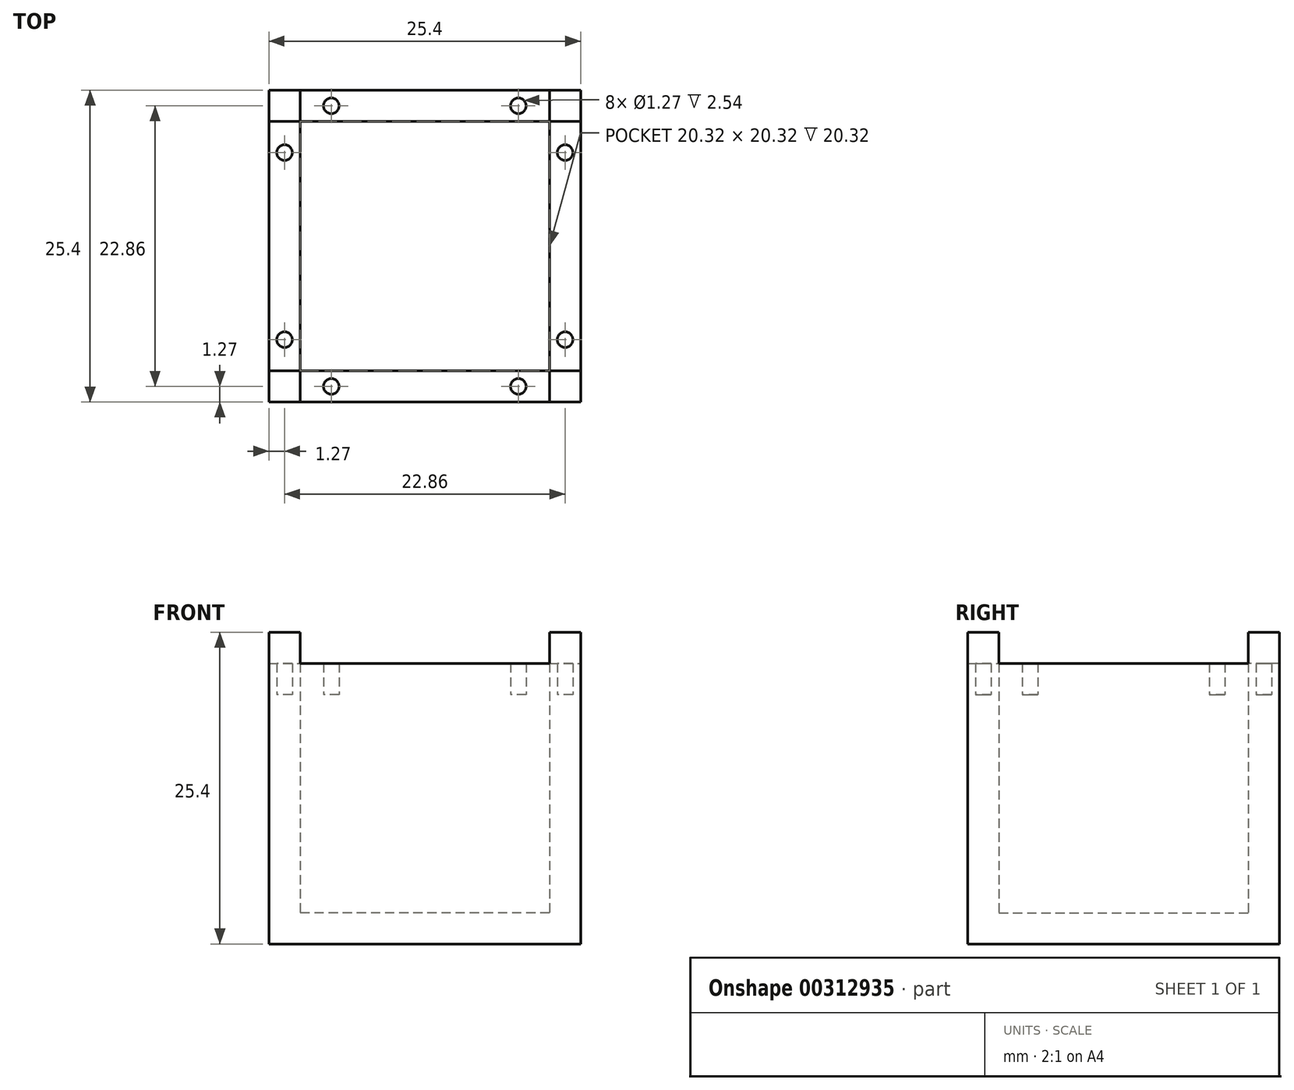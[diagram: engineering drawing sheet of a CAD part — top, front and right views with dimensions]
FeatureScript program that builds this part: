
annotation { "Feature Type Name" : "Feature", "Feature Type Description" : "" }
export const myFeature = defineFeature(function(context is Context, id is Id, definition is map)
    precondition{}
    {
        {
            var Q0;
            Q0=qCreatedBy(makeId("Top.planeOp"),FACE);
            var sketch = newSketch(context, id + "F0", { "sketchPlane" : qUnion([Q0])});
            skLineSegment(sketch, "E0.bottom", {"start": v(12.7, -12.7) * mm, "end": v(-12.7, -12.7) * mm});
            skLineSegment(sketch, "E0.top", {"start": v(12.7, 12.7) * mm, "end": v(-12.7, 12.7) * mm});
            skLineSegment(sketch, "E0.left", {"start": v(12.7, -12.7) * mm, "end": v(12.7, 12.7) * mm});
            skLineSegment(sketch, "E0.right", {"start": v(-12.7, -12.7) * mm, "end": v(-12.7, 12.7) * mm});
            skPoint(sketch, "E0.middle", {"position": v(0, 0) * mm});
            skLineSegment(sketch, "E1.bottom", {"start": v(10.16, -10.16) * mm, "end": v(-10.16, -10.16) * mm});
            skLineSegment(sketch, "E1.top", {"start": v(10.16, 10.16) * mm, "end": v(-10.16, 10.16) * mm});
            skLineSegment(sketch, "E1.left", {"start": v(10.16, -10.16) * mm, "end": v(10.16, 10.16) * mm});
            skLineSegment(sketch, "E1.right", {"start": v(-10.16, -10.16) * mm, "end": v(-10.16, 10.16) * mm});
            skLineSegment(sketch, "E2", {"start": v(-10.16, 10.16) * mm, "end": v(-10.16, 12.7) * mm});
            skLineSegment(sketch, "E3", {"start": v(-10.16, 10.16) * mm, "end": v(-12.7, 10.16) * mm});
            skLineSegment(sketch, "E4", {"start": v(-12.7, 10.16) * mm, "end": v(-12.7, 12.7) * mm});
            skLineSegment(sketch, "E5", {"start": v(10.16, 10.16) * mm, "end": v(10.16, 12.7) * mm});
            skLineSegment(sketch, "E6", {"start": v(10.16, 12.7) * mm, "end": v(12.7, 12.7) * mm});
            skLineSegment(sketch, "E7", {"start": v(12.7, 10.16) * mm, "end": v(10.16, 10.16) * mm});
            skLineSegment(sketch, "E8.bottom", {"start": v(-10.16, -10.16) * mm, "end": v(-12.7, -10.16) * mm});
            skLineSegment(sketch, "E8.top", {"start": v(-10.16, -12.7) * mm, "end": v(-12.7, -12.7) * mm});
            skLineSegment(sketch, "E8.left", {"start": v(-10.16, -10.16) * mm, "end": v(-10.16, -12.7) * mm});
            skLineSegment(sketch, "E8.right", {"start": v(-12.7, -10.16) * mm, "end": v(-12.7, -12.7) * mm});
            skLineSegment(sketch, "E9.bottom", {"start": v(10.16, -10.16) * mm, "end": v(12.7, -10.16) * mm});
            skLineSegment(sketch, "E9.top", {"start": v(10.16, -12.7) * mm, "end": v(12.7, -12.7) * mm});
            skLineSegment(sketch, "E9.left", {"start": v(10.16, -10.16) * mm, "end": v(10.16, -12.7) * mm});
            skLineSegment(sketch, "E9.right", {"start": v(12.7, -10.16) * mm, "end": v(12.7, -12.7) * mm});
            skSolve(sketch);
        }
        {
            var Q0;
            Q0=makeQuery(id+"F0.imprint","IMPRINT",FACE,{"disambiguationData":[TD([[makeQuery(id+"F0.imprint","IMPRINT",EDGE,{"derivedFrom":sQuery(id+"F0.wireOp",EDGE,"E1.bottom")}),-1.0]])]});
            extrude(context, id + "F1", {"entities" : qUnion([Q0]), "depth" : 2.54 * mm});
        }
        {
            var Q0;
            Q0=makeQuery(id+"F0.imprint","IMPRINT",FACE,{"disambiguationData":[TD([[makeQuery(id+"F0.imprint","IMPRINT",EDGE,{"derivedFrom":sQuery(id+"F0.wireOp",EDGE,"E0.right")}),-1.0]])]});
            var Q1;
            {var subQ2=sQuery(id+"F0.wireOp",EDGE,"E2");Q1=makeQuery(id+"F0.imprint","IMPRINT",FACE,{"disambiguationData":[TD([[makeQuery(id+"F0.imprint","IMPRINT",EDGE,{"derivedFrom":subQ2}),1.0]])]});}
            var Q2;
            Q2=makeQuery(id+"F0.imprint","IMPRINT",FACE,{"disambiguationData":[TD([[makeQuery(id+"F0.imprint","IMPRINT",EDGE,{"derivedFrom":sQuery(id+"F0.wireOp",EDGE,"E1.top")}),-1.0]])]});
            var Q3;
            Q3=makeQuery(id+"F0.imprint","IMPRINT",FACE,{"disambiguationData":[TD([[makeQuery(id+"F0.imprint","IMPRINT",EDGE,{"derivedFrom":sQuery(id+"F0.wireOp",EDGE,"E5")}),-1.0]])]});
            var Q4;
            Q4=makeQuery(id+"F0.imprint","IMPRINT",FACE,{"disambiguationData":[TD([[makeQuery(id+"F0.imprint","IMPRINT",EDGE,{"derivedFrom":sQuery(id+"F0.wireOp",EDGE,"E1.left")}),-1.0]])]});
            var Q5;
            Q5=makeQuery(id+"F0.imprint","IMPRINT",FACE,{"disambiguationData":[TD([[makeQuery(id+"F0.imprint","IMPRINT",EDGE,{"derivedFrom":sQuery(id+"F0.wireOp",EDGE,"E9.bottom")}),-1.0]])]});
            var Q6;
            Q6=makeQuery(id+"F0.imprint","IMPRINT",FACE,{"disambiguationData":[TD([[makeQuery(id+"F0.imprint","IMPRINT",EDGE,{"derivedFrom":sQuery(id+"F0.wireOp",EDGE,"E0.bottom")}),-1.0]])]});
            var Q7;
            Q7=makeQuery(id+"F0.imprint","IMPRINT",FACE,{"disambiguationData":[TD([[makeQuery(id+"F0.imprint","IMPRINT",EDGE,{"derivedFrom":sQuery(id+"F0.wireOp",EDGE,"E8.bottom")}),1.0]])]});
            extrude(context, id + "F2", {"entities" : qUnion([Q0, Q1, Q2, Q3, Q4, Q5, Q6, Q7]), "operationType" : NewBodyOperationType.ADD, "depth" : 22.86 * mm});
        }
        {
            var Q0;
            Q0=makeQuery(id+"F0.imprint","IMPRINT",FACE,{"disambiguationData":[TD([[makeQuery(id+"F0.imprint","IMPRINT",EDGE,{"derivedFrom":sQuery(id+"F0.wireOp",EDGE,"E8.bottom")}),1.0]])]});
            var Q1;
            Q1=makeQuery(id+"F0.imprint","IMPRINT",FACE,{"disambiguationData":[TD([[makeQuery(id+"F0.imprint","IMPRINT",EDGE,{"derivedFrom":sQuery(id+"F0.wireOp",EDGE,"E9.bottom")}),-1.0]])]});
            var Q2;
            Q2=makeQuery(id+"F0.imprint","IMPRINT",FACE,{"disambiguationData":[TD([[makeQuery(id+"F0.imprint","IMPRINT",EDGE,{"derivedFrom":sQuery(id+"F0.wireOp",EDGE,"E5")}),-1.0]])]});
            var Q3;
            {var subQ2=sQuery(id+"F0.wireOp",EDGE,"E2");Q3=makeQuery(id+"F0.imprint","IMPRINT",FACE,{"disambiguationData":[TD([[makeQuery(id+"F0.imprint","IMPRINT",EDGE,{"derivedFrom":subQ2}),1.0]])]});}
            extrude(context, id + "F3", {"entities" : qUnion([Q0, Q1, Q2, Q3]), "operationType" : NewBodyOperationType.ADD, "depth" : 25.4 * mm});
        }
        {
            var Q0;
            Q0=qCreatedBy(makeId("Top.planeOp"),FACE);
            var sketch = newSketch(context, id + "F4", { "sketchPlane" : qUnion([Q0])});
            skPoint(sketch, "E10.middle", {"position": v(0, 0) * mm});
            skCircle(sketch, "E11", {"center": v(-7.62, 11.43) * mm, "radius": 0.64 * mm});
            skCircle(sketch, "E12", {"center": v(7.62, 11.43) * mm, "radius": 0.64 * mm});
            skCircle(sketch, "E13", {"center": v(-11.43, 7.62) * mm, "radius": 0.64 * mm});
            skCircle(sketch, "E14", {"center": v(-11.43, -7.62) * mm, "radius": 0.64 * mm});
            skCircle(sketch, "E15", {"center": v(-7.62, -11.43) * mm, "radius": 0.64 * mm});
            skCircle(sketch, "E16", {"center": v(7.62, -11.43) * mm, "radius": 0.64 * mm});
            skCircle(sketch, "E17", {"center": v(11.43, 7.62) * mm, "radius": 0.64 * mm});
            skCircle(sketch, "E18", {"center": v(11.43, -7.62) * mm, "radius": 0.64 * mm});
            skSolve(sketch);
        }
        {
            var Q0;
            Q0=makeQuery(id+"F4.imprint","IMPRINT",FACE,{"disambiguationData":[TD([[makeQuery(id+"F4.imprint","IMPRINT",EDGE,{"derivedFrom":sQuery(id+"F4.wireOp",EDGE,"E15")}),1.0]])]});
            var Q1;
            Q1=makeQuery(id+"F4.imprint","IMPRINT",FACE,{"disambiguationData":[TD([[makeQuery(id+"F4.imprint","IMPRINT",EDGE,{"derivedFrom":sQuery(id+"F4.wireOp",EDGE,"E16")}),1.0]])]});
            var Q2;
            Q2=makeQuery(id+"F4.imprint","IMPRINT",FACE,{"disambiguationData":[TD([[makeQuery(id+"F4.imprint","IMPRINT",EDGE,{"derivedFrom":sQuery(id+"F4.wireOp",EDGE,"E18")}),1.0]])]});
            var Q3;
            Q3=makeQuery(id+"F4.imprint","IMPRINT",FACE,{"disambiguationData":[TD([[makeQuery(id+"F4.imprint","IMPRINT",EDGE,{"derivedFrom":sQuery(id+"F4.wireOp",EDGE,"E17")}),1.0]])]});
            var Q4;
            Q4=makeQuery(id+"F4.imprint","IMPRINT",FACE,{"disambiguationData":[TD([[makeQuery(id+"F4.imprint","IMPRINT",EDGE,{"derivedFrom":sQuery(id+"F4.wireOp",EDGE,"E12")}),1.0]])]});
            var Q5;
            Q5=makeQuery(id+"F4.imprint","IMPRINT",FACE,{"disambiguationData":[TD([[makeQuery(id+"F4.imprint","IMPRINT",EDGE,{"derivedFrom":sQuery(id+"F4.wireOp",EDGE,"E11")}),1.0]])]});
            var Q6;
            Q6=makeQuery(id+"F4.imprint","IMPRINT",FACE,{"disambiguationData":[TD([[makeQuery(id+"F4.imprint","IMPRINT",EDGE,{"derivedFrom":sQuery(id+"F4.wireOp",EDGE,"E13")}),1.0]])]});
            var Q7;
            Q7=makeQuery(id+"F4.imprint","IMPRINT",FACE,{"disambiguationData":[TD([[makeQuery(id+"F4.imprint","IMPRINT",EDGE,{"derivedFrom":sQuery(id+"F4.wireOp",EDGE,"E14")}),1.0]])]});
            extrude(context, id + "F5", {"entities" : qUnion([Q0, Q1, Q2, Q3, Q4, Q5, Q6, Q7]), "operationType" : NewBodyOperationType.REMOVE, "depth" : 25.4 * mm});
        }
        {
            var Q0;
            Q0 = qSketchRegion(id + "F0", true);
            extrude(context, id + "F6", {"entities" : qUnion([Q0]), "operationType" : NewBodyOperationType.ADD, "depth" : 20.32 * mm});
        }
    });
